# Revit family: ADB Gas Range cookers L1000
name_source: partatom
category: Equipement spécialisé
units: mm (PartAtom-declared; Revit-internal decimal feet)

## family parameters
Basée sur le plan de construction = Non
Conserver l'orientation des annotations = Non
Cote de connecteur circulaire = Utiliser le diamètre
Couper avec des vides une fois chargée = Non
Numéro OmniClass = 23.40.40.14.17.11
Partagée = Non
Repère de localisation dans la pièce = Non
Titre OmniClass = Cookers, Ovens, Stoves
Toujours verticalement = Oui
Type d'élément = Normal

## types (2) — shared parameters
Commentaires du type = Ambassade range - Gas range cookers
Fabricant = Société Industrielle de Lacanche
Gas Size = 21 mm
Pbase = 0 W
Pbase gaz = 26 W
URL = https://www.ambassade-de-bourgogne.com
zero-valued in all types: Elévation par défaut

## per-type parameters (varying)
| type | Description | Modèle | Plaques | Weight |
| 5 Gas burners - 2 ovens - CG 1052 B | Gas range cooker 5 Gas burners - 2 ovens - CG 1052 B | CG 1052 P | CG1052CF_CG1052P_Fourneaux 4-5 feux vifs : CG1052 P | 124.00 kg |
| 4 Gas burners - 1 Cast iron simmer plate - 2 ovens - CG 1052 CF | Gas range cooker 4 Gas burners  - 1 Cast iron simmer plate - 2 ovens - CG 1052 CF | CG 1052 CF | CG1052CF_CG1052P_Fourneaux 4-5 feux vifs : CG1052 CF | 127.00 kg |
